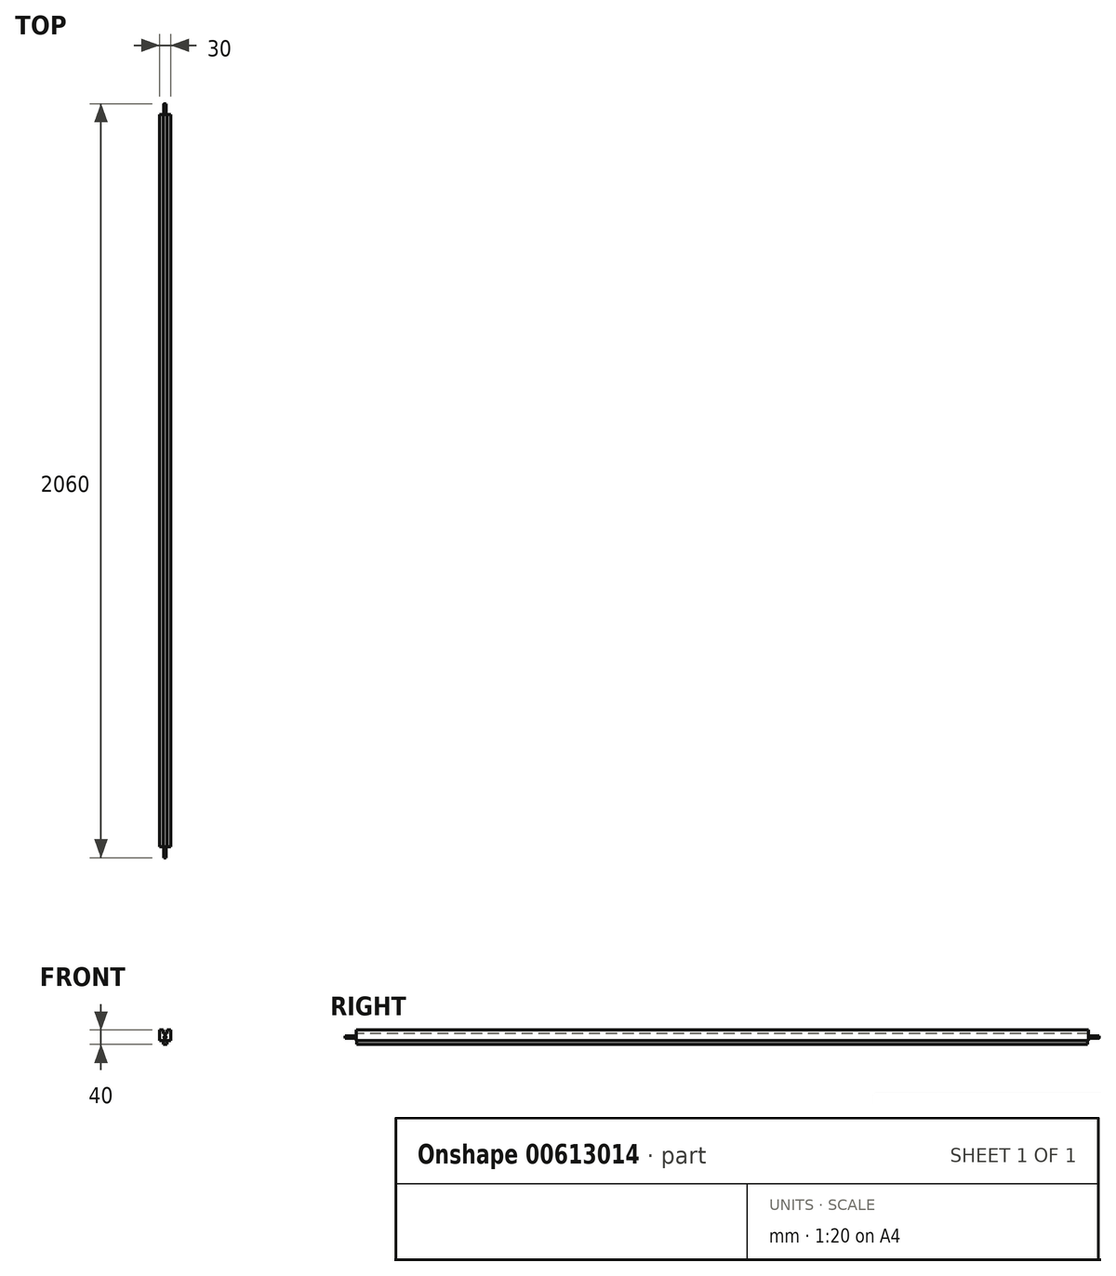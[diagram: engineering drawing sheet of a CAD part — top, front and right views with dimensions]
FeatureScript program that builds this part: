
annotation { "Feature Type Name" : "Feature", "Feature Type Description" : "" }
export const myFeature = defineFeature(function(context is Context, id is Id, definition is map)
    precondition{}
    {
        {
            var Q0;
            Q0=qCreatedBy(makeId("Right.planeOp"),FACE);
            var sketch = newSketch(context, id + "F0", { "sketchPlane" : qUnion([Q0])});
            skLineSegment(sketch, "E0.bottom", {"start": v(1000, -10) * mm, "end": v(-1000, -10) * mm});
            skLineSegment(sketch, "E0.top", {"start": v(1000, 10) * mm, "end": v(-1000, 10) * mm});
            skLineSegment(sketch, "E0.left", {"start": v(1000, -10) * mm, "end": v(1000, 10) * mm});
            skLineSegment(sketch, "E0.right", {"start": v(-1000, -10) * mm, "end": v(-1000, 10) * mm});
            skPoint(sketch, "E0.middle", {"position": v(0, 0) * mm});
            skSolve(sketch);
        }
        {
            var Q0;
            Q0=qSketchRegion(id+"F0",true);
            extrude(context, id + "F1", {"entities" : qUnion([Q0]), "depth" : 30 * mm, "offsetDistance" : 25 * mm});
        }
        {
            var Q0;
            Q0=makeQuery(id+"F1.opExtrude","SWEPT_FACE",FACE,{"disambiguationData":[OSD([sQuery(id+"F0.wireOp",EDGE,"E0.right")])]});
            var sketch = newSketch(context, id + "F2", { "sketchPlane" : qUnion([Q0])});
            skLineSegment(sketch, "E1.bottom", {"start": v(10, 10) * mm, "end": v(0, 10) * mm});
            skLineSegment(sketch, "E1.top", {"start": v(10, 20) * mm, "end": v(0, 20) * mm});
            skLineSegment(sketch, "E1.left", {"start": v(10, 10) * mm, "end": v(10, 20) * mm});
            skLineSegment(sketch, "E1.right", {"start": v(0, 10) * mm, "end": v(0, 20) * mm});
            skPoint(sketch, "E1.middle", {"position": v(5, 15) * mm});
            skSolve(sketch);
        }
        {
            var Q0;
            Q0=qSketchRegion(id+"F2",true);
            extrude(context, id + "F3", {"entities" : qUnion([Q0]), "operationType" : NewBodyOperationType.ADD, "depth" : -2000 * mm, "offsetDistance" : 25 * mm});
        }
        {
            var Q0;
            Q0=makeQuery(id+"F3.boolean.opBoolean","MERGE",FACE,{"derivedFrom":[makeQuery(id+"F1.opExtrude","SWEPT_FACE",FACE,{"disambiguationData":[OSD([sQuery(id+"F0.wireOp",EDGE,"E0.right")])]}),makeQuery(id+"F3.opExtrude","CAP_FACE",FACE,{"disambiguationData":[OSD([sQuery(id+"F2.wireOp",EDGE,"E1.bottom"),sQuery(id+"F2.wireOp",EDGE,"E1.top"),sQuery(id+"F2.wireOp",EDGE,"E1.left"),sQuery(id+"F2.wireOp",EDGE,"E1.right")])],"isStart":true})]});
            var sketch = newSketch(context, id + "F4", { "sketchPlane" : qUnion([Q0])});
            skLineSegment(sketch, "E2.bottom", {"start": v(30, 10) * mm, "end": v(20, 10) * mm});
            skLineSegment(sketch, "E2.top", {"start": v(30, 20) * mm, "end": v(20, 20) * mm});
            skLineSegment(sketch, "E2.left", {"start": v(30, 10) * mm, "end": v(30, 20) * mm});
            skLineSegment(sketch, "E2.right", {"start": v(20, 10) * mm, "end": v(20, 20) * mm});
            skPoint(sketch, "E2.middle", {"position": v(25, 15) * mm});
            skSolve(sketch);
        }
        {
            var Q0;
            Q0=qSketchRegion(id+"F4",true);
            extrude(context, id + "F5", {"entities" : qUnion([Q0]), "operationType" : NewBodyOperationType.ADD, "depth" : -2000 * mm, "offsetDistance" : 25 * mm});
        }
        {
            var Q0;
            Q0=makeQuery(id+"F5.boolean.opBoolean","MERGE",FACE,{"derivedFrom":[makeQuery(id+"F3.boolean.opBoolean","MERGE",FACE,{"derivedFrom":[makeQuery(id+"F1.opExtrude","SWEPT_FACE",FACE,{"disambiguationData":[OSD([sQuery(id+"F0.wireOp",EDGE,"E0.right")])]}),makeQuery(id+"F3.opExtrude","CAP_FACE",FACE,{"disambiguationData":[OSD([sQuery(id+"F2.wireOp",EDGE,"E1.bottom"),sQuery(id+"F2.wireOp",EDGE,"E1.top"),sQuery(id+"F2.wireOp",EDGE,"E1.left"),sQuery(id+"F2.wireOp",EDGE,"E1.right")])],"isStart":true})]}),makeQuery(id+"F5.opExtrude","CAP_FACE",FACE,{"disambiguationData":[OSD([sQuery(id+"F4.wireOp",EDGE,"E2.bottom"),sQuery(id+"F4.wireOp",EDGE,"E2.top"),sQuery(id+"F4.wireOp",EDGE,"E2.left"),sQuery(id+"F4.wireOp",EDGE,"E2.right")])],"isStart":true})]});
            var sketch = newSketch(context, id + "F6", { "sketchPlane" : qUnion([Q0])});
            skLineSegment(sketch, "E3.bottom", {"start": v(20, -20) * mm, "end": v(10, -20) * mm});
            skLineSegment(sketch, "E3.top", {"start": v(20, -10) * mm, "end": v(10, -10) * mm});
            skLineSegment(sketch, "E3.left", {"start": v(20, -20) * mm, "end": v(20, -10) * mm});
            skLineSegment(sketch, "E3.right", {"start": v(10, -20) * mm, "end": v(10, -10) * mm});
            skPoint(sketch, "E3.middle", {"position": v(15, -15) * mm});
            skSolve(sketch);
        }
        {
            var Q0;
            Q0=qSketchRegion(id+"F6",true);
            extrude(context, id + "F7", {"entities" : qUnion([Q0]), "operationType" : NewBodyOperationType.ADD, "oppositeDirection" : true, "depth" : 1998 * mm, "offsetDistance" : 25 * mm, "hasSecondDirection" : true, "secondDirectionOppositeDirection" : true, "secondDirectionDepth" : 2 * mm});
        }
        {
            var Q0;
            Q0=makeQuery(id+"F7.boolean.opBoolean","MERGE",FACE,{"derivedFrom":[makeQuery(id+"F5.boolean.opBoolean","MERGE",FACE,{"derivedFrom":[makeQuery(id+"F3.boolean.opBoolean","MERGE",FACE,{"derivedFrom":[makeQuery(id+"F1.opExtrude","SWEPT_FACE",FACE,{"disambiguationData":[OSD([sQuery(id+"F0.wireOp",EDGE,"E0.right")])]}),makeQuery(id+"F3.opExtrude","CAP_FACE",FACE,{"disambiguationData":[OSD([sQuery(id+"F2.wireOp",EDGE,"E1.bottom"),sQuery(id+"F2.wireOp",EDGE,"E1.top"),sQuery(id+"F2.wireOp",EDGE,"E1.left"),sQuery(id+"F2.wireOp",EDGE,"E1.right")])],"isStart":true})]}),makeQuery(id+"F5.opExtrude","CAP_FACE",FACE,{"disambiguationData":[OSD([sQuery(id+"F4.wireOp",EDGE,"E2.bottom"),sQuery(id+"F4.wireOp",EDGE,"E2.top"),sQuery(id+"F4.wireOp",EDGE,"E2.left"),sQuery(id+"F4.wireOp",EDGE,"E2.right")])],"isStart":true})]}),makeQuery(id+"F7.opExtrude","CAP_FACE",FACE,{"disambiguationData":[OSD([sQuery(id+"F6.wireOp",EDGE,"E3.bottom"),sQuery(id+"F6.wireOp",EDGE,"E3.top"),sQuery(id+"F6.wireOp",EDGE,"E3.left"),sQuery(id+"F6.wireOp",EDGE,"E3.right")])],"isStart":true})]});
            var sketch = newSketch(context, id + "F8", { "sketchPlane" : qUnion([Q0])});
            skCircle(sketch, "E4", {"center": v(15, 0) * mm, "radius": 3 * mm});
            skSolve(sketch);
        }
        {
            var Q0;
            Q0 = qSketchRegion(id + "F8", true);
            extrude(context, id + "F9", {"entities" : qUnion([Q0]), "operationType" : NewBodyOperationType.ADD, "depth" : 30 * mm, "offsetDistance" : 25 * mm});
        }
        {
            var Q0;
            Q0=makeQuery(id+"F7.boolean.opBoolean","MERGE",FACE,{"derivedFrom":[makeQuery(id+"F5.boolean.opBoolean","MERGE",FACE,{"derivedFrom":[makeQuery(id+"F3.boolean.opBoolean","MERGE",FACE,{"derivedFrom":[makeQuery(id+"F1.opExtrude","SWEPT_FACE",FACE,{"disambiguationData":[OSD([sQuery(id+"F0.wireOp",EDGE,"E0.left")])]}),makeQuery(id+"F3.opExtrude","CAP_FACE",FACE,{"disambiguationData":[OSD([sQuery(id+"F2.wireOp",EDGE,"E1.bottom"),sQuery(id+"F2.wireOp",EDGE,"E1.top"),sQuery(id+"F2.wireOp",EDGE,"E1.left"),sQuery(id+"F2.wireOp",EDGE,"E1.right")])],"isStart":false})]}),makeQuery(id+"F5.opExtrude","CAP_FACE",FACE,{"disambiguationData":[OSD([sQuery(id+"F4.wireOp",EDGE,"E2.bottom"),sQuery(id+"F4.wireOp",EDGE,"E2.top"),sQuery(id+"F4.wireOp",EDGE,"E2.left"),sQuery(id+"F4.wireOp",EDGE,"E2.right")])],"isStart":false})]}),makeQuery(id+"F7.opExtrude","CAP_FACE",FACE,{"disambiguationData":[OSD([sQuery(id+"F6.wireOp",EDGE,"E3.bottom"),sQuery(id+"F6.wireOp",EDGE,"E3.top"),sQuery(id+"F6.wireOp",EDGE,"E3.left"),sQuery(id+"F6.wireOp",EDGE,"E3.right")])],"isStart":false})]});
            var sketch = newSketch(context, id + "F10", { "sketchPlane" : qUnion([Q0])});
            skCircle(sketch, "E5", {"center": v(-15, 0) * mm, "radius": 3 * mm});
            skSolve(sketch);
        }
        {
            var Q0;
            Q0 = qSketchRegion(id + "F10", true);
            extrude(context, id + "F11", {"entities" : qUnion([Q0]), "operationType" : NewBodyOperationType.ADD, "depth" : 30 * mm, "offsetDistance" : 25 * mm});
        }
    });
